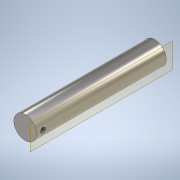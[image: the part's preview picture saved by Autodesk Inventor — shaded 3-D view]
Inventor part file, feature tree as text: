
AUTODESK INVENTOR PART (.ipt)
format: ipt  version: 2020 (Build 240168000, 168)  size: 106,496 bytes
history: native  units: mm
features: sketch x2, extrude x1, plane x1, hole x1
ambient origin geometry x8: Origin, YZ Plane, XZ Plane, XY Plane, X Axis, Y Axis, Z Axis, Center Point
bodies: Solid1 (feature_tree)
feature tree (5):
  extrude  "Extrusion1"  Depth=40.0mm TaperAngle=0.0deg
  plane  "Work Plane1"
  hole  "Hole1"  [1 undecoded]
  sketch  "Sketch1"  dims[d0=7.0mm d1=40.0mm d2=0.0mm]
  sketch  "Sketch2"  dims[d3=1.5mm d4=6.0mm d5=4.0mm d6=2.0mm d7=90.0deg d8=3.5mm d9=20.594885mm]
note: 1 required parameter value undecoded (feature->parameter linkage not recoverable at this tier; creation-order binding heuristic only, values carry confidence <= 0.55)
